# Revit family: DC_Rheem_PLM_Raypak_B3694ID
name_source: partatom
category: Plumbing Fixtures
revit_build: Autodesk Revit 2017 (Build: 20160225_1515(x64)
units: mm (PartAtom-declared; Revit-internal decimal feet)

## family parameters
Cut with Voids When Loaded = No
Host = Face
Part Type = Normal
Room Calculation Point = No
Round Connector Dimension = Use Radius
Shared = No

## types (4) — shared parameters
ColdWaterPipeDiameter_ANZRS = 80 mm
ColdWaterPipeRadius_ANZRS = 40 mm  [stored 0.131234 ft]
Height_ANZRS = 1738 mm
HotWaterPipeDiameter_ANZRS = 80 mm
HotWaterPipeRadius_ANZRS = 40 mm  [stored 0.131234 ft]
Manufacturer = Raypak
Material_ANZRS = Raypak - Grey Powder Coated Steel
PRVRadius_ANZRS = 20 mm  [stored 0.0656168 ft]
TopDiameter_ANZRS = 760 mm
TopWidth_ANZRS = 1445 mm
URL = http://www.rheem.com.au
Width_ANZRS = 2350 mm
zero-valued in all types: Default Elevation

## per-type parameters (varying)
| type | GasPipeDiameter_ANZRS | GasPipeRadius_ANZRS | Model | Type Comments |
| Raypak - Gas Water Heater- Indoor - 3692 MJ/h  Natural gas, modulating gas control | 80 mm | 40 mm  [stored 0.131234 ft] | B3694NCM/ID | Recovery 14448L/h @ 50oC rise |
| Raypak - Gas Water Heater- Indoor - 3692 MJ/h  Natural gas, On/Off gas control | 80 mm | 40 mm  [stored 0.131234 ft] | B3694NCO/ID | Recovery 14448L/h @ 50oC rise |
| Raypak - Gas Water Heater- Indoor - 3540 MJ/h  Propane gas, modulating gas control | 40 mm  [stored 0.131234 ft] | 20 mm  [stored 0.0656168 ft] | B3694PCM/ID | Recovery 13588L/h @ 50oC rise |
| Raypak - Gas Water Heater- Indoor - 3540 MJ/h  Propane gas, On/Off gas control | 40 mm  [stored 0.131234 ft] | 20 mm  [stored 0.0656168 ft] | B3694PCO/ID | Recovery 13588L/h @ 50oC rise |

note: column(s) folded — value = type name in every type: Description

note: [stored X ft] marks values corroborated as IEEE doubles in the binary element streams (Revit-internal decimal feet)

## geometry (parser evidence)
native form markers: Blend x6, Sweep x2
no freeform markers — native parametric forms only
